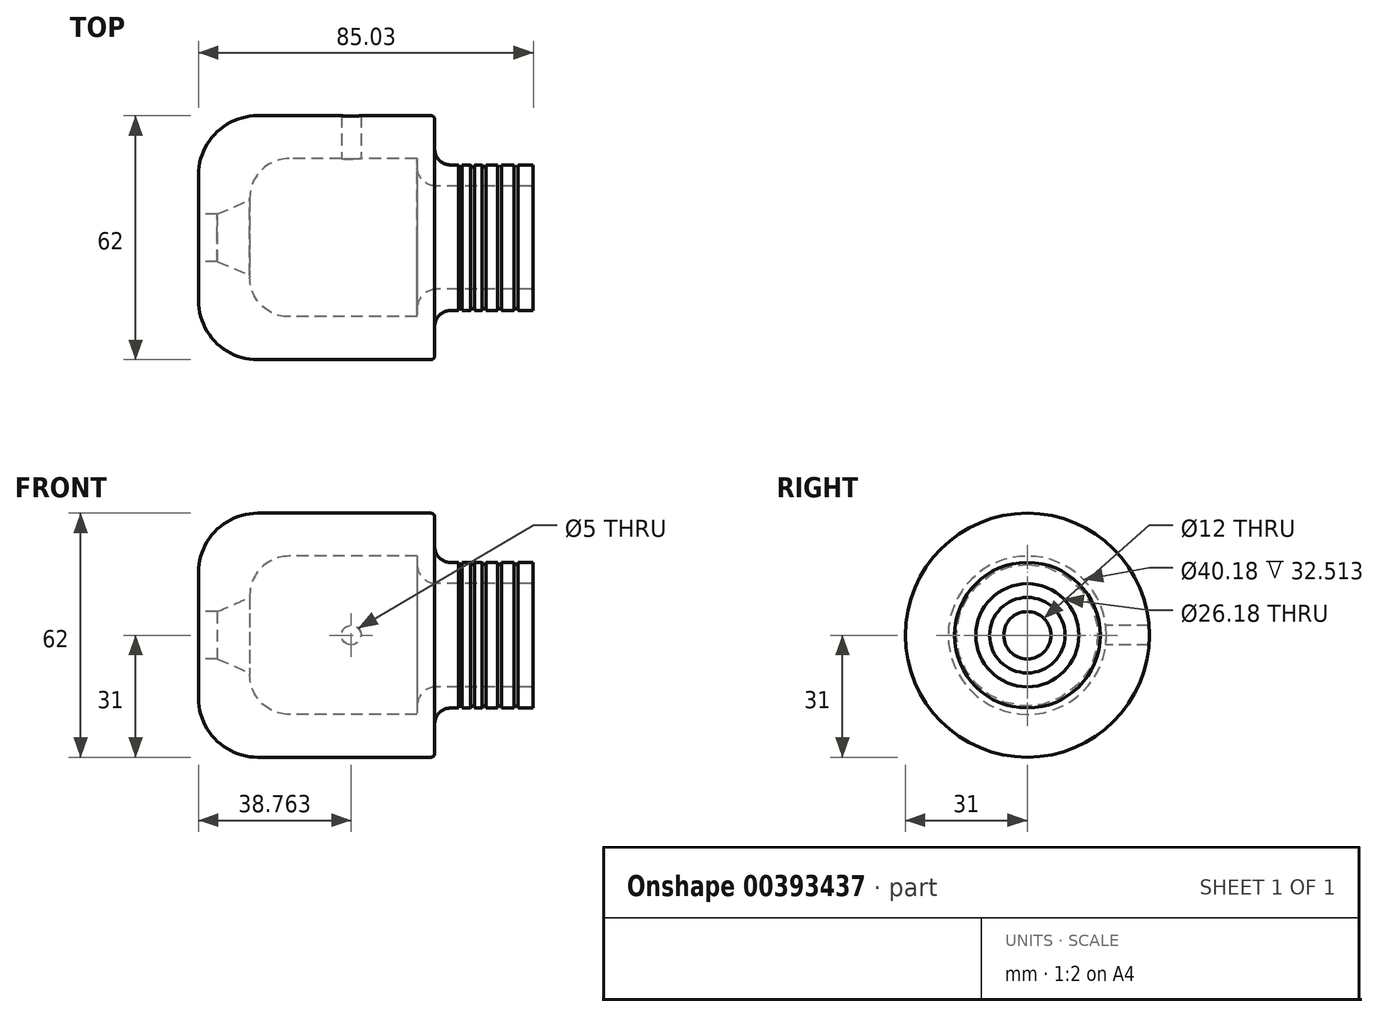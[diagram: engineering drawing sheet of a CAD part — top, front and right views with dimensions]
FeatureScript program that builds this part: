
annotation { "Feature Type Name" : "Feature", "Feature Type Description" : "" }
export const myFeature = defineFeature(function(context is Context, id is Id, definition is map)
    precondition{}
    {
        {
            var Q0;
            Q0=qCreatedBy(makeId("Front.planeOp"),FACE);
            var sketch = newSketch(context, id + "F0", { "sketchPlane" : qUnion([Q0])});
            skLineSegment(sketch, "E0.bottom", {"start": v(15, 31) * mm, "end": v(59, 31) * mm});
            skLineSegment(sketch, "E0.left", {"start": v(0, 16) * mm, "end": v(0, 6) * mm});
            skLineSegment(sketch, "E0.right", {"start": v(60, 30) * mm, "end": v(60, 22.5) * mm});
            skLineSegment(sketch, "E1", {"start": v(0, 0) * mm, "end": v(79.05, 0) * mm});
            skLineSegment(sketch, "E2.bottom", {"start": v(64, 18.5) * mm, "end": v(66, 18.5) * mm});
            skPoint(sketch, "E3.visualSharp", {"position": v(0, 31) * mm});
            skArc(sketch, "E3.filletArc", {"start": v(15, 31) * mm, "mid": v(4.4, 26.6) * mm, "end": v(0, 16) * mm});
            skLineSegment(sketch, "E4.bottom", {"start": v(23, 20.09) * mm, "end": v(55.52, 20.09) * mm});
            skLineSegment(sketch, "E4.right", {"start": v(55.52, 20.09) * mm, "end": v(55.52, 18.09) * mm});
            skLineSegment(sketch, "E5.bottom", {"start": v(60.52, 13.09) * mm, "end": v(84.53, 13.09) * mm});
            skLineSegment(sketch, "E5.top", {"start": v(85, 6.1) * mm, "end": v(85.07, 6.1) * mm});
            skPoint(sketch, "E6.visualSharp", {"position": v(13.52, 20.09) * mm});
            skArc(sketch, "E6.filletArc", {"start": v(23, 20.09) * mm, "mid": v(15.76, 16.98) * mm, "end": v(13.02, 9.59) * mm});
            skPoint(sketch, "E7.visualSharp", {"position": v(55.52, 13.09) * mm});
            skArc(sketch, "E7.filletArc", {"start": v(55.52, 18.09) * mm, "mid": v(56.98, 14.55) * mm, "end": v(60.52, 13.09) * mm});
            skLineSegment(sketch, "E8.trimOffspring", {"start": v(85, 6.1) * mm, "end": v(85, 6) * mm});
            skLineSegment(sketch, "E9", {"start": v(85, 18.5) * mm, "end": v(85.03, 13.6) * mm});
            skPoint(sketch, "E10.visualSharp", {"position": v(60, 18.5) * mm});
            skArc(sketch, "E10.filletArc", {"start": v(60, 22.5) * mm, "mid": v(61.17, 19.67) * mm, "end": v(64, 18.5) * mm});
            skPoint(sketch, "E11.visualSharp", {"position": v(60, 31) * mm});
            skArc(sketch, "E11.filletArc", {"start": v(60, 30) * mm, "mid": v(59.7, 30.7) * mm, "end": v(59, 31) * mm});
            skLineSegment(sketch, "E12", {"start": v(0, 6) * mm, "end": v(4.74, 6) * mm});
            skLineSegment(sketch, "E13", {"start": v(4.74, 6) * mm, "end": v(13.02, 9.59) * mm});
            skArc(sketch, "E14", {"start": v(66, 18.5) * mm, "mid": v(66.5, 18) * mm, "end": v(67, 18.5) * mm});
            skArc(sketch, "E15", {"start": v(69.14, 18.5) * mm, "mid": v(69.64, 18) * mm, "end": v(70.14, 18.5) * mm});
            skArc(sketch, "E16", {"start": v(72.06, 18.5) * mm, "mid": v(72.56, 18) * mm, "end": v(73.06, 18.5) * mm});
            skArc(sketch, "E17", {"start": v(75.95, 18.5) * mm, "mid": v(76.45, 18) * mm, "end": v(76.95, 18.5) * mm});
            skArc(sketch, "E18", {"start": v(80.15, 18.5) * mm, "mid": v(80.65, 18) * mm, "end": v(81.15, 18.5) * mm});
            skLineSegment(sketch, "E19.trimOffspring", {"start": v(67, 18.5) * mm, "end": v(69.14, 18.5) * mm});
            skLineSegment(sketch, "E20.trimOffspring", {"start": v(70.14, 18.5) * mm, "end": v(72.06, 18.5) * mm});
            skLineSegment(sketch, "E21.trimOffspring", {"start": v(73.06, 18.5) * mm, "end": v(75.95, 18.5) * mm});
            skLineSegment(sketch, "E22.trimOffspring", {"start": v(76.95, 18.5) * mm, "end": v(80.15, 18.5) * mm});
            skLineSegment(sketch, "E23.trimOffspring", {"start": v(81.15, 18.5) * mm, "end": v(85, 18.5) * mm});
            skArc(sketch, "E24.filletArc", {"start": v(84.53, 13.09) * mm, "mid": v(84.88, 13.24) * mm, "end": v(85.03, 13.6) * mm});
            skSolve(sketch);
        }
        {
            var Q0;
            Q0=makeQuery(id+"F0.imprint","IMPRINT",FACE,{"disambiguationData":[TD([[makeQuery(id+"F0.imprint","IMPRINT",EDGE,{"derivedFrom":sQuery(id+"F0.wireOp",EDGE,"E0.bottom")}),-1.0]])]});
            var Q1;
            Q1=sQuery(id+"F0.wireOp",EDGE,"E1");
            revolve(context, id + "F1", {"entities" : qUnion([Q0]), "axis" : qUnion([Q1]), "revolveType" : RevolveType.FULL});
        }
        {
            var Q0;
            Q0=qCreatedBy(makeId("Front.planeOp"),FACE);
            var sketch = newSketch(context, id + "F2", { "sketchPlane" : qUnion([Q0])});
            skCircle(sketch, "E25", {"center": v(38.76, 0) * mm, "radius": 2.5 * mm});
            skSolve(sketch);
        }
        {
            var Q0;
            Q0 = qSketchRegion(id + "F2", true);
            var Q1;
            Q1=sQuery(id+"F2.wireOp",EDGE,"E25");
            extrude(context, id + "F3", {"entities" : qUnion([Q0]), "operationType" : NewBodyOperationType.REMOVE, "surfaceEntities" : qUnion([Q1]), "endBound" : BoundingType.THROUGH_ALL, "oppositeDirection" : true, "depth" : 60 * mm});
        }
    });
